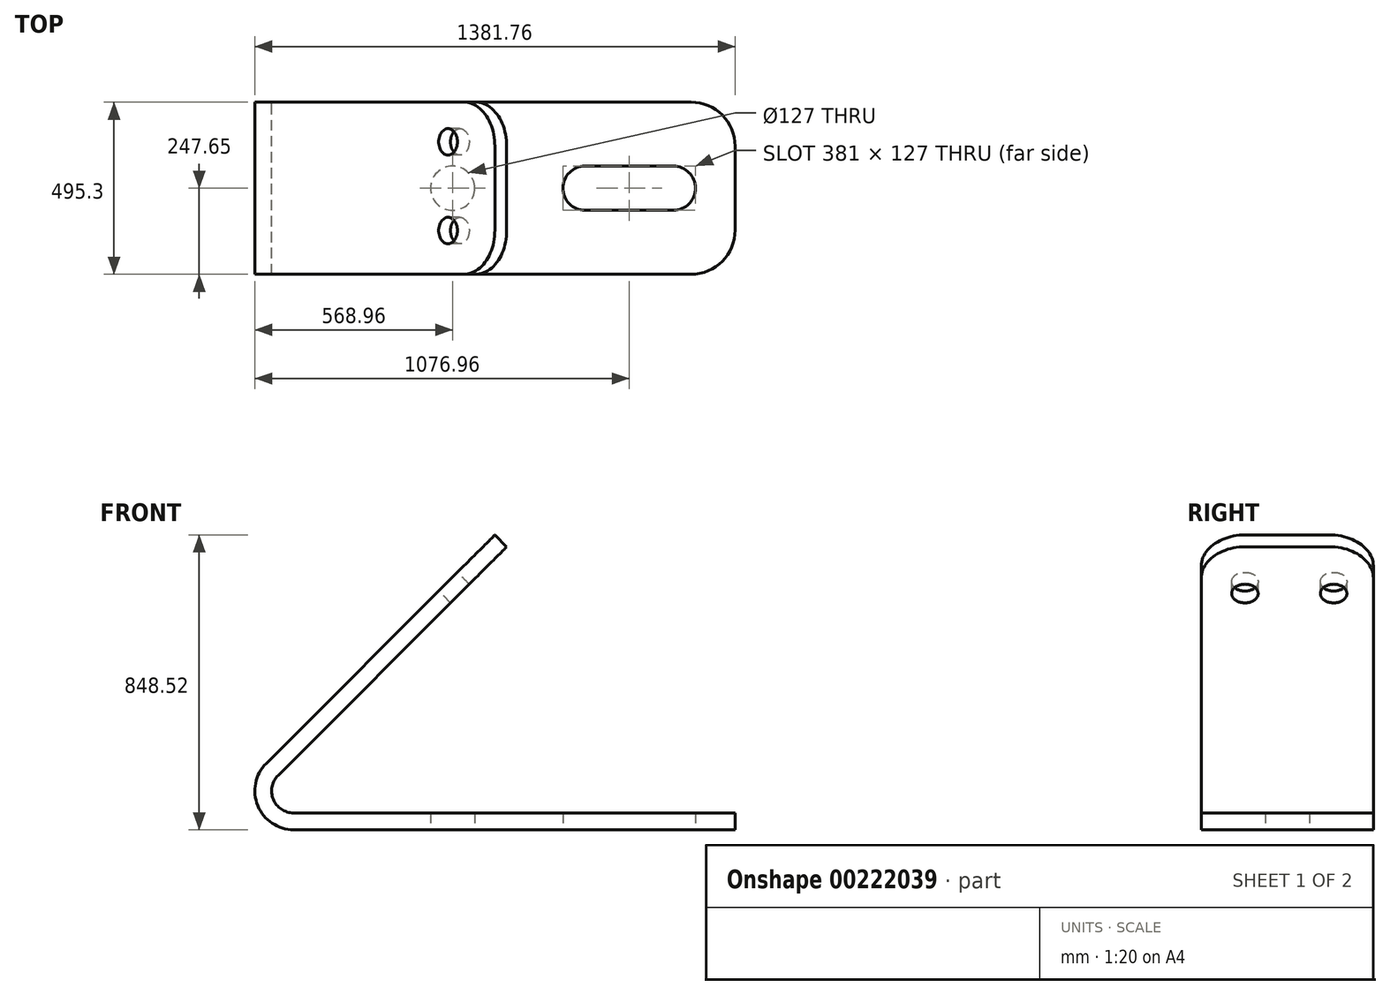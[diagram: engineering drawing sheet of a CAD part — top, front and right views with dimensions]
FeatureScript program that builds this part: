
annotation { "Feature Type Name" : "Feature", "Feature Type Description" : "" }
export const myFeature = defineFeature(function(context is Context, id is Id, definition is map)
    precondition{}
    {
        {
            var Q0;
            Q0=qCreatedBy(makeId("Front.planeOp"),FACE);
            var sketch = newSketch(context, id + "F0", { "sketchPlane" : qUnion([Q0])});
            skArc(sketch, "E0", {"start": v(-79.03, 79.03) * mm, "mid": v(-103.25, -42.77) * mm, "end": v(0, -111.76) * mm});
            skLineSegment(sketch, "E1", {"start": v(0, -111.76) * mm, "end": v(1270, -111.76) * mm});
            skLineSegment(sketch, "E2", {"start": v(-79.03, 79.03) * mm, "end": v(578.7, 736.76) * mm});
            skLineSegment(sketch, "E3", {"start": v(1270, -111.76) * mm, "end": v(1270, -63.5) * mm});
            skLineSegment(sketch, "E4", {"start": v(1270, -63.5) * mm, "end": v(0, -63.5) * mm});
            skLineSegment(sketch, "E5", {"start": v(578.7, 736.76) * mm, "end": v(612.83, 702.63) * mm});
            skLineSegment(sketch, "E6", {"start": v(612.83, 702.63) * mm, "end": v(-44.9, 44.9) * mm});
            skArc(sketch, "E7", {"start": v(-44.9, 44.9) * mm, "mid": v(-58.67, -24.3) * mm, "end": v(0, -63.5) * mm});
            skSolve(sketch);
        }
        {
            var Q0;
            Q0=makeQuery(id+"F0.imprint","IMPRINT",FACE,{"disambiguationData":[TD([[makeQuery(id+"F0.imprint","IMPRINT",EDGE,{"derivedFrom":sQuery(id+"F0.wireOp",EDGE,"E0")}),1.0]])]});
            extrude(context, id + "F1", {"entities" : qUnion([Q0]), "endBound" : BoundingType.SYMMETRIC, "depth" : 495.3 * mm});
        }
        {
            var Q0;
            Q0=makeQuery(id+"F1.opExtrude","SWEPT_FACE",FACE,{"disambiguationData":[OSD([sQuery(id+"F0.wireOp",EDGE,"E2")])]});
            var sketch = newSketch(context, id + "F2", { "sketchPlane" : qUnion([Q0])});
            skCircle(sketch, "E8", {"center": v(-133.35, 739.68) * mm, "radius": 38.1 * mm});
            skCircle(sketch, "E9.1.0.0", {"center": v(121.92, 739.68) * mm, "radius": 38.1 * mm});
            skLineSegment(sketch, "E9.direction1", {"start": v(-133.35, 739.68) * mm, "end": v(121.92, 739.68) * mm, "construction": true});
            skSolve(sketch);
        }
        {
            var Q0;
            Q0=makeQuery(id+"F2.imprint","IMPRINT",FACE,{"disambiguationData":[TD([[makeQuery(id+"F2.imprint","IMPRINT",EDGE,{"derivedFrom":sQuery(id+"F2.wireOp",EDGE,"E8")}),1.0]])]});
            var Q1;
            Q1=makeQuery(id+"F2.imprint","IMPRINT",FACE,{"disambiguationData":[TD([[makeQuery(id+"F2.imprint","IMPRINT",EDGE,{"derivedFrom":sQuery(id+"F2.wireOp",EDGE,"E9.1.0.0")}),1.0]])]});
            extrude(context, id + "F3", {"entities" : qUnion([Q0, Q1]), "operationType" : NewBodyOperationType.REMOVE, "oppositeDirection" : true, "depth" : 50.8 * mm});
        }
        {
            var Q0;
            Q0=makeQuery(id+"F1.opExtrude","SWEPT_FACE",FACE,{"disambiguationData":[OSD([sQuery(id+"F0.wireOp",EDGE,"E1")])]});
            var sketch = newSketch(context, id + "F4", { "sketchPlane" : qUnion([Q0])});
            skPoint(sketch, "E10.endSnap0", {"position": v(1270, 0) * mm});
            skLineSegment(sketch, "E11.bottom", {"start": v(1092.2, -63.5) * mm, "end": v(838.2, -63.5) * mm});
            skLineSegment(sketch, "E11.top", {"start": v(1092.2, 63.5) * mm, "end": v(838.2, 63.5) * mm});
            skCircle(sketch, "E12", {"center": v(457.2, 0) * mm, "radius": 63.5 * mm});
            skArc(sketch, "E13", {"start": v(838.2, 63.5) * mm, "mid": v(774.7, 0) * mm, "end": v(838.2, -63.5) * mm});
            skArc(sketch, "E14.1.0.0", {"start": v(1092.2, -63.5) * mm, "mid": v(1155.7, 0) * mm, "end": v(1092.2, 63.5) * mm});
            skLineSegment(sketch, "E14.direction1", {"start": v(838.2, 0) * mm, "end": v(1092.2, 0) * mm, "construction": true});
            skPoint(sketch, "E15.orphan", {"position": v(774.7, 63.5) * mm});
            skPoint(sketch, "E16.orphan", {"position": v(774.7, -63.5) * mm});
            skPoint(sketch, "E17.orphan", {"position": v(1155.7, -63.5) * mm});
            skLineSegment(sketch, "E18.trimOffspring", {"start": v(774.7, 0) * mm, "end": v(104.87, 0) * mm, "construction": true});
            skSolve(sketch);
        }
        {
            var Q0;
            Q0=makeQuery(id+"F4.imprint","IMPRINT",FACE,{"disambiguationData":[TD([[makeQuery(id+"F4.imprint","IMPRINT",EDGE,{"derivedFrom":sQuery(id+"F4.wireOp",EDGE,"E11.bottom")}),-1.0]])]});
            var Q1;
            Q1=makeQuery(id+"F4.imprint","IMPRINT",FACE,{"disambiguationData":[TD([[makeQuery(id+"F4.imprint","IMPRINT",EDGE,{"derivedFrom":sQuery(id+"F4.wireOp",EDGE,"E12")}),1.0]])]});
            extrude(context, id + "F5", {"entities" : qUnion([Q0, Q1]), "operationType" : NewBodyOperationType.REMOVE, "oppositeDirection" : true, "depth" : 50.8 * mm});
        }
        {
            var Q0;
            Q0=makeQuery(id+"F1.opExtrude","CAP_EDGE",EDGE,{"disambiguationData":[OSD([sQuery(id+"F0.wireOp",EDGE,"E3")])],"isStart":false});
            var Q1;
            Q1=makeQuery(id+"F1.opExtrude","CAP_EDGE",EDGE,{"disambiguationData":[OSD([sQuery(id+"F0.wireOp",EDGE,"E3")])],"isStart":true});
            var Q2;
            Q2=makeQuery(id+"F1.opExtrude","CAP_EDGE",EDGE,{"disambiguationData":[OSD([sQuery(id+"F0.wireOp",EDGE,"E5")])],"isStart":false});
            var Q3;
            Q3=makeQuery(id+"F1.opExtrude","CAP_EDGE",EDGE,{"disambiguationData":[OSD([sQuery(id+"F0.wireOp",EDGE,"E5")])],"isStart":true});
            fillet(context, id + "F6", {"entities" : qUnion([Q0, Q1, Q2, Q3]), "radius" : 127 * mm, "tangentPropagation" : true, "allowEdgeOverflow" : false});
        }
    });
